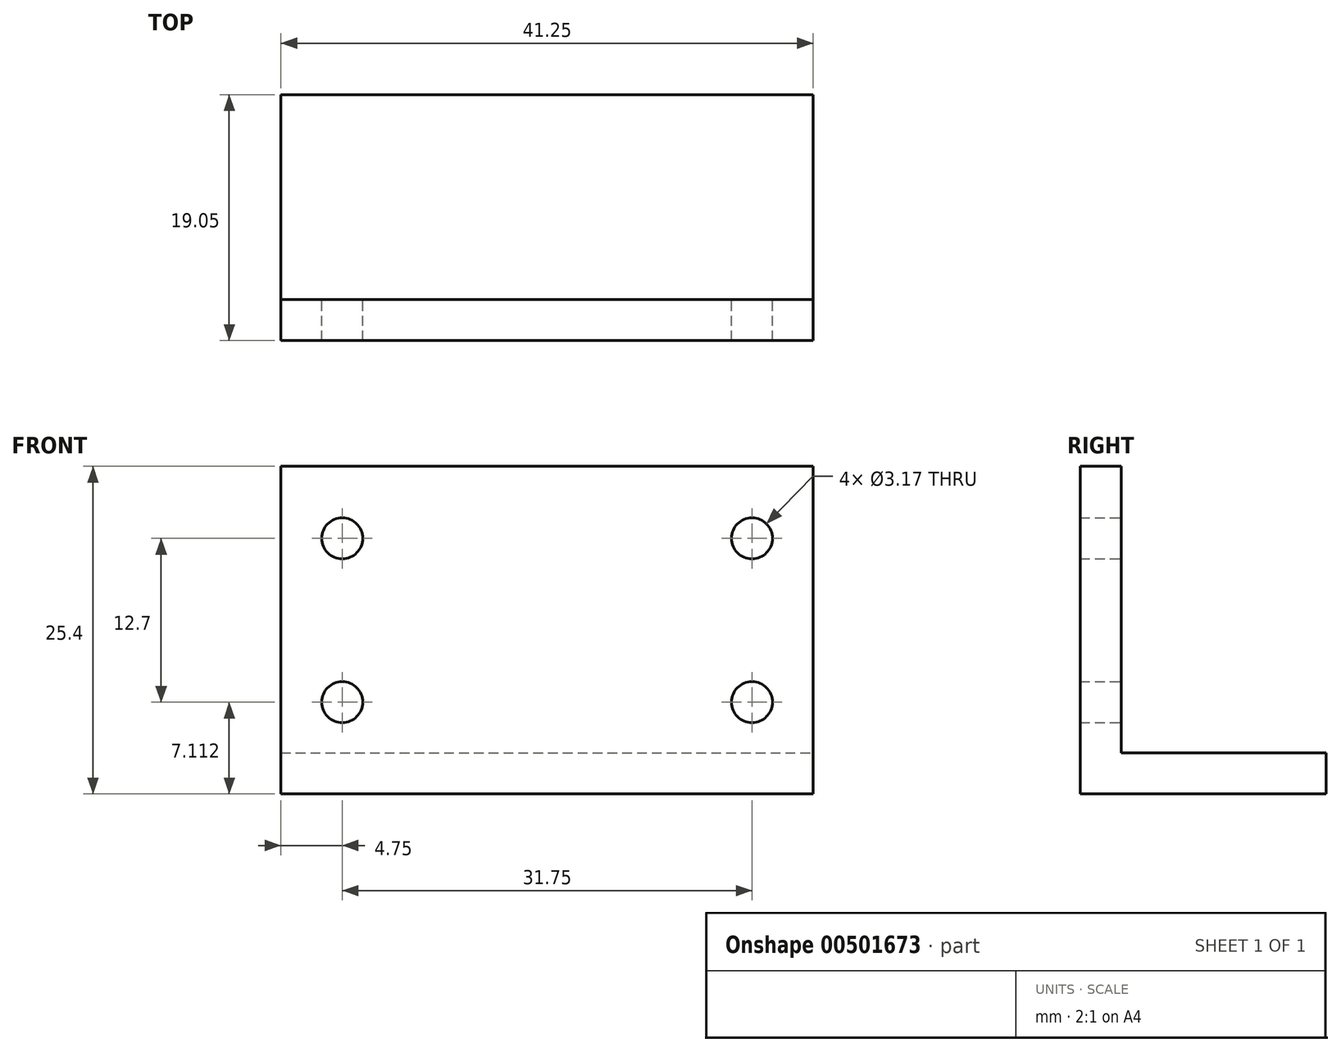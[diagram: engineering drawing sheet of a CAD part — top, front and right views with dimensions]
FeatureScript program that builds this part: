
annotation { "Feature Type Name" : "Feature", "Feature Type Description" : "" }
export const myFeature = defineFeature(function(context is Context, id is Id, definition is map)
    precondition{}
    {
        {
            var Q0;
            Q0=qCreatedBy(makeId("Right.planeOp"),FACE);
            var sketch = newSketch(context, id + "F0", { "sketchPlane" : qUnion([Q0])});
            skLineSegment(sketch, "E0", {"start": v(0, 25.4) * mm, "end": v(3.18, 25.4) * mm});
            skLineSegment(sketch, "E1", {"start": v(3.18, 25.4) * mm, "end": v(3.18, 3.17) * mm});
            skLineSegment(sketch, "E2", {"start": v(3.18, 3.17) * mm, "end": v(19.05, 3.17) * mm});
            skLineSegment(sketch, "E3", {"start": v(19.05, 3.17) * mm, "end": v(19.05, 0) * mm});
            skLineSegment(sketch, "E4", {"start": v(19.05, 0) * mm, "end": v(0, 0) * mm});
            skLineSegment(sketch, "E5", {"start": v(0, 0) * mm, "end": v(0, 25.4) * mm});
            skSolve(sketch);
        }
        {
            var Q0;
            Q0 = qSketchRegion(id + "F0", true);
            extrude(context, id + "F1", {"entities" : qUnion([Q0]), "oppositeDirection" : true, "depth" : 41.25 * mm, "offsetDistance" : 25.4 * mm});
        }
        {
            var Q0;
            Q0=makeQuery(id+"F1.opExtrude","SWEPT_FACE",FACE,{"disambiguationData":[OSD([sQuery(id+"F0.wireOp",EDGE,"E1")])]});
            var sketch = newSketch(context, id + "F2", { "sketchPlane" : qUnion([Q0])});
            skCircle(sketch, "E6", {"center": v(4.75, 19.81) * mm, "radius": 1.59 * mm});
            skCircle(sketch, "E7", {"center": v(36.5, 19.81) * mm, "radius": 1.59 * mm});
            skCircle(sketch, "E8", {"center": v(4.75, 7.11) * mm, "radius": 1.59 * mm});
            skCircle(sketch, "E9", {"center": v(36.5, 7.11) * mm, "radius": 1.59 * mm});
            skSolve(sketch);
        }
        {
            var Q0;
            Q0 = qSketchRegion(id + "F2", true);
            extrude(context, id + "F3", {"entities" : qUnion([Q0]), "operationType" : NewBodyOperationType.REMOVE, "endBound" : BoundingType.THROUGH_ALL, "oppositeDirection" : true, "depth" : 25.4 * mm});
        }
    });
